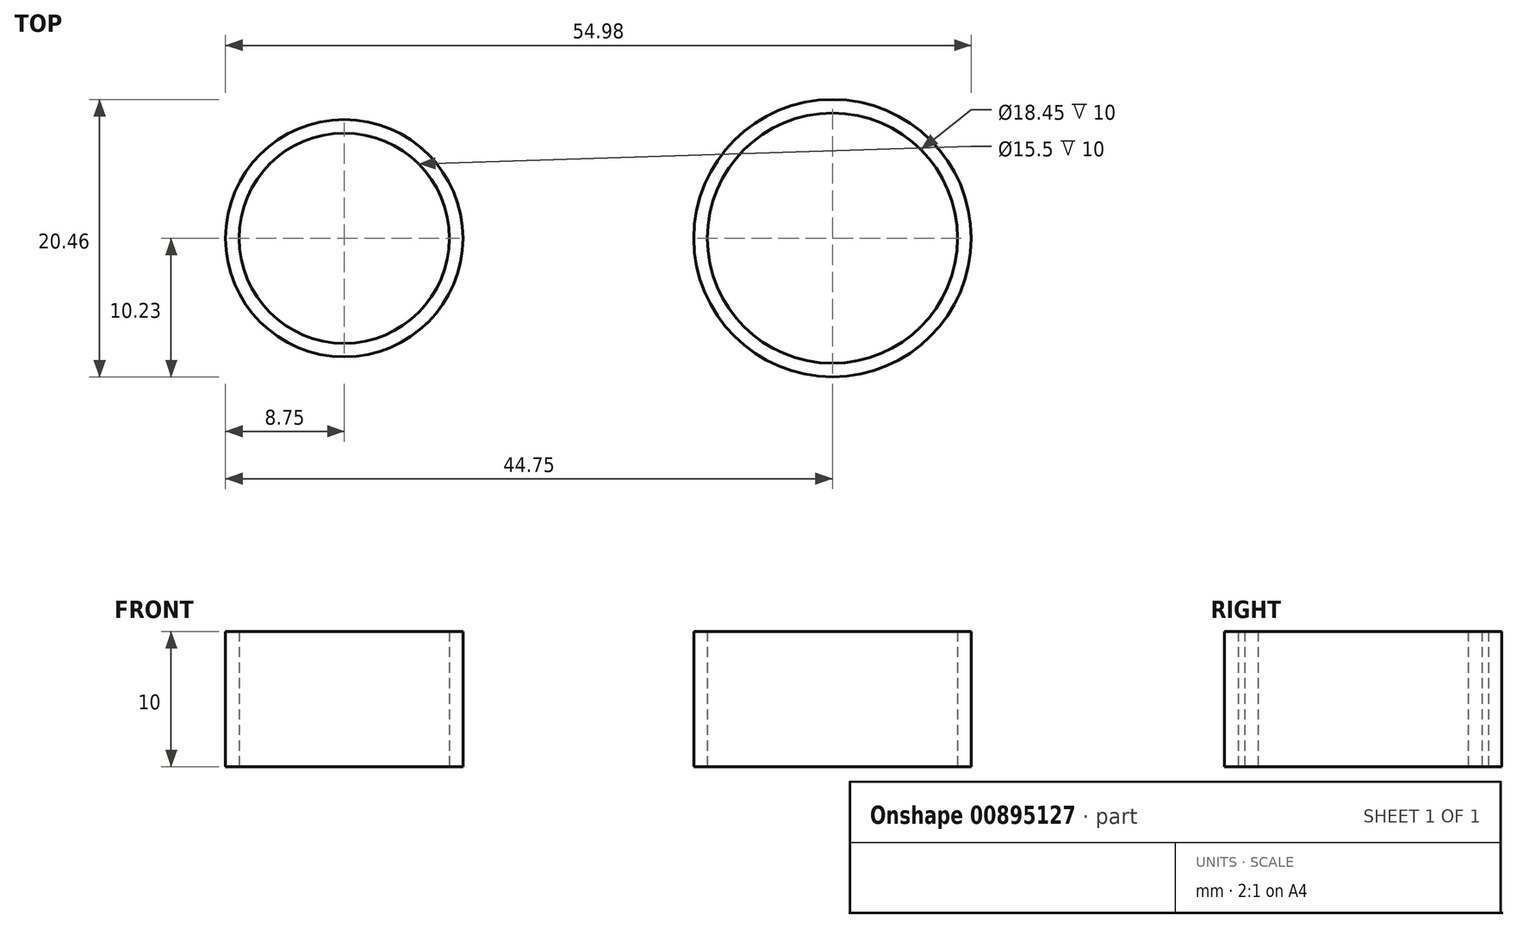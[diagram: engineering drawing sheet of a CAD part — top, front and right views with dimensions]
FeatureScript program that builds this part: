
annotation { "Feature Type Name" : "Feature", "Feature Type Description" : "" }
export const myFeature = defineFeature(function(context is Context, id is Id, definition is map)
    precondition{}
    {
        {
            var Q0;
            Q0=qCreatedBy(makeId("Top.planeOp"),FACE);
            var sketch = newSketch(context, id + "F0", { "sketchPlane" : qUnion([Q0])});
            skLineSegment(sketch, "E0.bottom", {"start": v(90, 90) * mm, "end": v(-90, 90) * mm, "construction": true});
            skLineSegment(sketch, "E0.top", {"start": v(90, -90) * mm, "end": v(-90, -90) * mm, "construction": true});
            skLineSegment(sketch, "E0.left", {"start": v(90, 90) * mm, "end": v(90, -90) * mm, "construction": true});
            skLineSegment(sketch, "E0.right", {"start": v(-90, 90) * mm, "end": v(-90, -90) * mm, "construction": true});
            skPoint(sketch, "E0.middle", {"position": v(0, 0) * mm});
            skCircle(sketch, "E1", {"center": v(0, 0) * mm, "radius": 9.23 * mm});
            skLineSegment(sketch, "E2.direction2", {"start": v(0, 0) * mm, "end": v(0, 36) * mm, "construction": true});
            skCircle(sketch, "E3.MirrorC", {"center": v(-36, 0) * mm, "radius": 7.75 * mm});
            skCircle(sketch, "E4.0", {"center": v(-36, 0) * mm, "radius": 8.75 * mm});
            skCircle(sketch, "E5.0", {"center": v(0, 0) * mm, "radius": 10.23 * mm});
            skSolve(sketch);
        }
        {
            var Q0;
            Q0=qSketchRegion(id+"F0",true);
            extrude(context, id + "F1", {"entities" : qUnion([Q0]), "depth" : 10 * mm, "offsetDistance" : 25 * mm});
        }
    });
